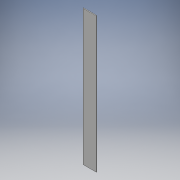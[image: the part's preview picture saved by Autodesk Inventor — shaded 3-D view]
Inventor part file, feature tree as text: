
AUTODESK INVENTOR PART (.ipt)
format: ipt  version: 2017 (Build 210142000, 142)  size: 91,648 bytes
history: native  units: mm
features: other x1, extrude x1, sketch x1
ambient origin geometry x8: Origin, YZ Plane, XZ Plane, XY Plane, X Axis, Y Axis, Z Axis, Center Point
bodies: Body1 (feature_tree)
feature tree (3):
  other  "Sólido1"
  extrude  "Extrusión1"  Depth=909.0mm
  sketch  "Boceto1"  dims[d0=88.9mm d1=909.0mm d2=5.0mm d3=0.0mm]
